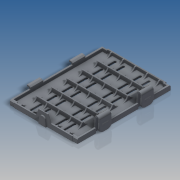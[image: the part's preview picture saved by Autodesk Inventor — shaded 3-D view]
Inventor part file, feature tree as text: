
AUTODESK INVENTOR PART (.ipt)
format: ipt  version: 2016 SP2 (Build 200236200, 236)  size: 2,044,928 bytes
history: native  units: in
note: dims shown in document units (in); Inventor stores cm internally (conversion verified against a paired STEP export)
features: extrude x13, sketch x6, pattern_linear x3, mirror x3, fillet x2, chamfer x1, plane x1
ambient origin geometry x8: Origin, YZ Plane, XZ Plane, XY Plane, X Axis, Y Axis, Z Axis, Center Point
bodies: Solid1 (feature_tree)
feature tree (29):
  sketch  "Sketch2"  dims[d0=2.1732in d1=2.5197in]
  extrude  "Extrusion1"  Depth=2.5197in
  extrude  "Extrusion2"  Depth=0.0157in
  extrude  "Extrusion3"  Depth=0.0472in
  sketch  "Sketch3"  dims[d2=3.4961in d3=0.0157in]
  extrude  "Extrusion4"  Depth=2.3937in
  extrude  "Extrusion5"  Depth=0.1575in
  extrude  "Extrusion6"  Depth=0.0315in
  pattern_linear  "Rectangular Pattern1"  Spacing1=0.4409in  [1 undecoded]
  mirror  "Mirror1"
  pattern_linear  "Rectangular Pattern2"  Spacing1=0.5669in  [1 undecoded]
  extrude  "Extrusion7"  Depth=0.0315in
  pattern_linear  "Rectangular Pattern3"  Spacing1=0.5157in  [1 undecoded]
  mirror  "Mirror2"
  chamfer  "Chamfer1"  Distance=0.126in
  sketch  "Sketch5"  dims[d6=0.6929in d7=2.3937in]
  extrude  "Extrusion8"  Depth=0.0315in
  extrude  "Extrusion9"  Depth=0.0315in
  plane  "Work Plane1"
  sketch  "Sketch6"  dims[d8=0.0472in d9=0.1575in]
  extrude  "Extrusion10"  Depth=0.0315in
  extrude  "Extrusion11"  Depth=0.0315in
  sketch  "Sketch7"  dims[d10=3.4016in d11=0.0787in d12=0.4409in d13=0.5669in d15=0.1024in d24=0.5157in d25=0.126in d26=0.7874in d28=0.315in d29=0.7874in d31=2.7559in d34=0.7874in d36=0.315in d37=1.5748in d39=0.5669in d42=0.7874in d44=0.9449in d45=0.3937in d47=0.3937in d49=0.1732in d50=0.0in d51=0.1102in d52=0.0in d53=0.1102in d54=0.0in d55=0.1969in d56=0.0472in d57=0.1417in d58=1.7323in d59=0.0in d60=0.0472in d61=0.0in d62=0.0472in d63=0.0in d64=0.7874in d66=0.3937in d67=1.9685in d69=0.5669in d70=0.1969in d71=0.0472in d72=0.0472in d73=0.0in d74=1.9685in d76=0.4488in d77=0.0315in d78=0.0787in d79=45.0deg d80=0.5669in d81=0.3465in d82=0.252in d83=0.2835in d86=0.1102in d87=0.0945in d88=0.315in d89=0.0315in d90=0.0in d91=0.0472in d92=0.0in d93=0.0945in d94=0.0472in d95=0.4724in d96=0.0472in d97=0.0472in d98=0.0472in d99=0.0787in d100=0.063in d101=0.4724in d102=0.0in d103=0.0472in d104=0.0157in d105=0.2047in d106=0.0787in d107=0.2205in d108=0.0in d109=0.4409in d110=0.1575in d111=0.2205in d112=0.0in d113=0.2205in d114=0.0in d115=0.0039in d116=0.0039in d117=0.0315in]
  extrude  "Extrusion12"  Depth=0.3937in
  extrude  "Extrusion13"  Depth=0.0315in TaperAngle=0.0deg
  mirror  "Mirror3"
  fillet  "Fillet1"  Radius=0.1102in
  fillet  "Fillet2"  Radius=0.1102in
  sketch  "Sketch4"  dims[d4=0.5039in d5=0.0472in]
note: 3 required parameter values undecoded (feature->parameter linkage not recoverable at this tier; creation-order binding heuristic only, values carry confidence <= 0.55)
